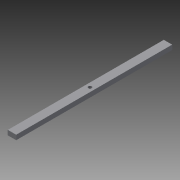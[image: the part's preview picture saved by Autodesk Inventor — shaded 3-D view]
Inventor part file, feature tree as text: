
AUTODESK INVENTOR PART (.ipt)
format: ipt  version: 2015 (Build 190159000, 159)  size: 76,288 bytes
history: native  units: in
note: dims shown in document units (in); Inventor stores cm internally (conversion verified against a paired STEP export)
features: extrude x1, sketch x1
ambient origin geometry x8: Origin, YZ Plane, XZ Plane, XY Plane, X Axis, Y Axis, Z Axis, Center Point
bodies: Solid1 (feature_tree)
feature tree (2):
  extrude  "Extrusion1"  Depth=0.5906in
  sketch  "Sketch1"  dims[d0=0.4724in d1=0.5906in d2=11.0236in d3=1.1811in d4=11.0236in d5=1.1811in d6=0.6693in d7=0.0in]
